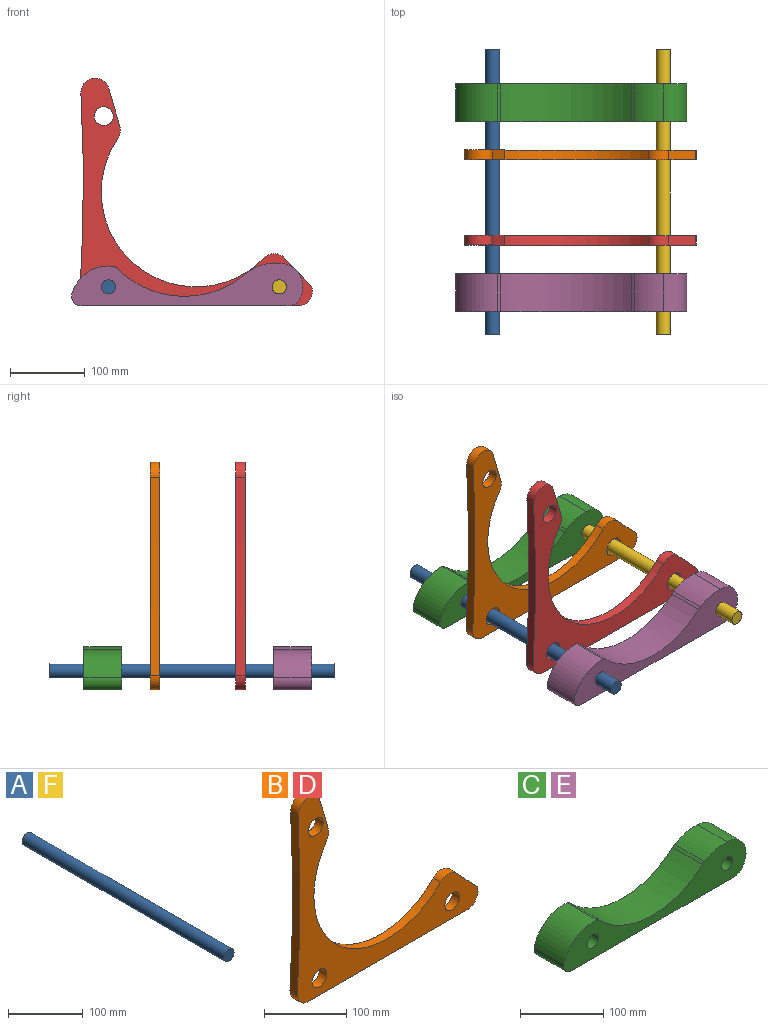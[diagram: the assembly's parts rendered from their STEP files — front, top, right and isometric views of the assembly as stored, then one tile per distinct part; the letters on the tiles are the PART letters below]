
ASSEMBLY  parts=6 mates=5
PART A: 3 faces, bbox 19.1x381x19.1 mm
  f0: cylinder r=9.53mm len=381mm, axis (0,1,0), area 22801.8mm2, adj f1,f2
  f1: plane 19.05x19.05mm, normal (0,-1,0), area 285mm2, adj f0
  f2: plane 19.05x19.05mm, normal (0,1,0), area 285mm2, adj f0
PART B: 15 faces, bbox 311.2x12.7x304.8 mm
  f0: cylinder r=19.05mm len=19.05mm, axis (0,1,0), area 380mm2, adj f1,f12,f13,f14
  f1: plane 273.05x12.7mm, normal (0,0,-1), area 3467.7mm2, adj f0,f2,f13,f14
  f2: cylinder r=19.05mm len=25.4mm, axis (0,1,0), area 462.2mm2, adj f1,f3,f13,f14
  f3: plane 38.39x35.77mm, normal (0.73,0,0.68), area 666.4mm2, adj f2,f4,f13,f14
  f4: cylinder r=19.05mm len=27.62mm, axis (0,1,0), area 392.4mm2, adj f3,f5,f13,f14
  f5: cylinder r=127mm len=218.23mm, axis (0,1,0), area 4795.7mm2, adj f4,f6,f13,f14
  f6: cylinder r=19.05mm len=16.1mm, axis (0,1,0), area 214mm2, adj f5,f7,f13,f14
  f7: plane 50.76x14.79mm, normal (0.96,0,0.28), area 671.4mm2, adj f6,f8,f13,f14
  f8: cylinder r=19.05mm len=37.34mm, axis (0,1,0), area 704.5mm2, adj f7,f12,f13,f14
  f9: cylinder r=12.7mm len=25.4mm, axis (0,1,0), area 1013.4mm2, adj f13,f14
  f10: cylinder r=12.7mm len=25.4mm, axis (0,1,0), area 1013.4mm2, adj f13,f14
  f11: cylinder r=12.7mm len=25.4mm, axis (0,1,0), area 1013.4mm2, adj f13,f14
  f12: cylinder r=2286mm len=265.68mm, axis (0,1,0), area 3376mm2, adj f0,f8,f13,f14
  f13: plane 311.15x304.8mm, normal (0,-1,0), area 21515.5mm2, adj f0,f1,f2,f3,f4,f5,f6,f7
  f14: plane 311.15x304.8mm, normal (0,1,0), area 21515.5mm2, adj f0,f1,f2,f3,f4,f5,f6,f7
PART C: 13 faces, bbox 309.8x50.8x57.4 mm
  f0: cylinder r=6.35mm len=50.8mm, axis (0,1,0), area 212.4mm2, adj f1,f10,f11,f12
  f1: cylinder r=50.8mm len=56.01mm, axis (0,1,0), area 3716.4mm2, adj f0,f2,f11,f12
  f2: cylinder r=12.7mm len=50.8mm, axis (0,1,0), area 1187.6mm2, adj f1,f3,f11,f12
  f3: plane 275.48x50.8mm, normal (0,0,-1), area 13994.4mm2, adj f2,f4,f11,f12
  f4: cylinder r=25.4mm len=50.8mm, axis (0,1,0), area 680.3mm2, adj f3,f5,f11,f12
  f5: cylinder r=31.75mm len=53.7mm, axis (0,1,0), area 3764.8mm2, adj f4,f6,f11,f12
  f6: cylinder r=63.5mm len=50.8mm, axis (0,1,0), area 2071.2mm2, adj f5,f7,f11,f12
  f7: cylinder r=25.4mm len=50.8mm, axis (0,1,0), area 217.2mm2, adj f6,f10,f11,f12
  f8: cylinder r=9.53mm len=50.8mm, axis (0,1,0), area 3040.2mm2, adj f11,f12
  f9: cylinder r=9.53mm len=50.8mm, axis (0,1,0), area 3040.2mm2, adj f11,f12
  f10: cylinder r=127mm len=175.55mm, axis (0,1,0), area 9853.4mm2, adj f0,f7,f11,f12
  f11: plane 309.77x57.36mm, normal (0,-1,0), area 10049.8mm2, adj f0,f1,f2,f3,f4,f5,f6,f7
  f12: plane 309.77x57.36mm, normal (0,1,0), area 10049.8mm2, adj f0,f1,f2,f3,f4,f5,f6,f7
PART D: same geometry as B
PART E: same geometry as C
PART F: same geometry as A
PLACE A t=(-103.19,-78.99,-68.76)mm
PLACE B t=(-141.29,-23.11,-94.16)mm
PLACE C t=(-141.29,65.79,-94.16)mm
PLACE D t=(-141.29,-137.41,-94.16)mm
PLACE E t=(-141.29,-188.21,-94.16)mm
PLACE F t=(125.41,-78.99,-68.76)mm
MATE planar C.f8 <-> B.f9  axis (0,1,0) through (-103.19,65.79,-68.76)mm
MATE slider A.f0 <-> E.f8  axis (0,-1,0) through (-103.19,-269.49,-68.76)mm
MATE slider F.f0 <-> E.f5  axis (0,-1,0) through (125.41,-269.49,-68.76)mm
MATE planar B.f9 <-> D.f9  axis (0,1,0) through (-103.19,-23.11,-68.76)mm
MATE planar E.f8 <-> D.f9  axis (0,-1,0) through (-103.19,-239.01,-68.76)mm
